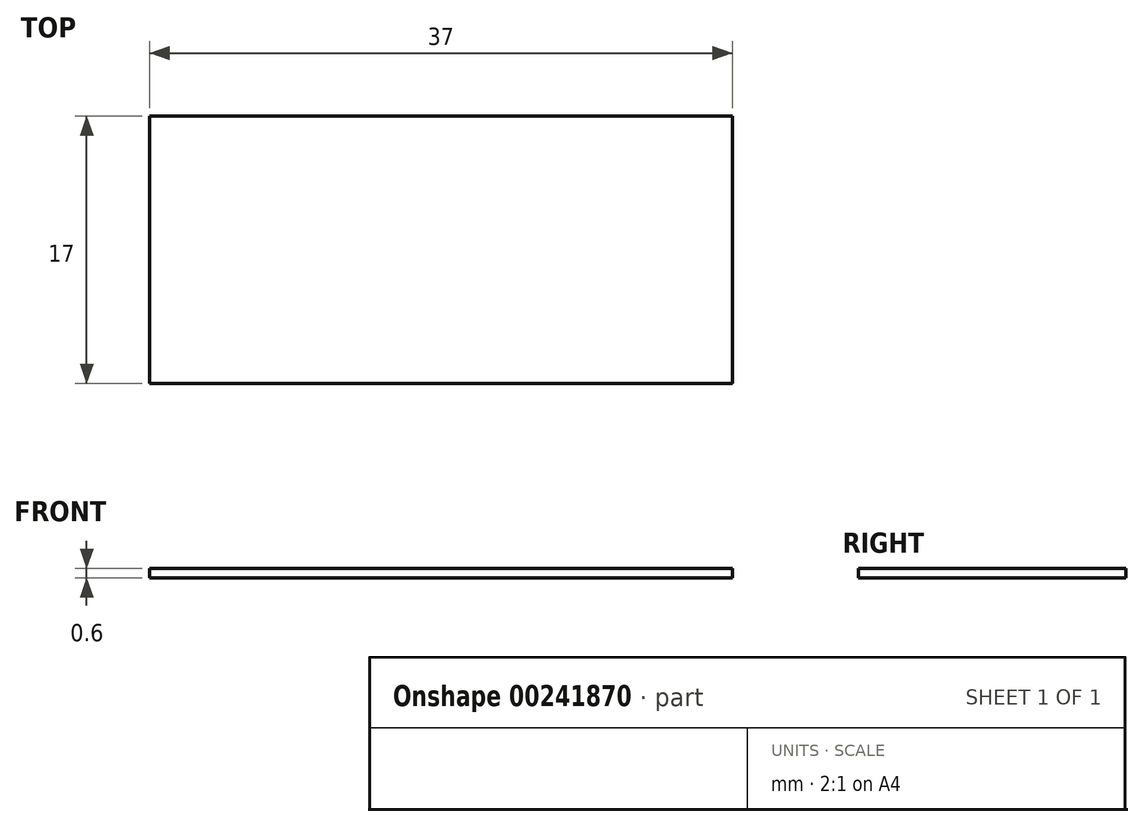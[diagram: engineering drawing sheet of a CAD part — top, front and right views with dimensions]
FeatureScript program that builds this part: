
annotation { "Feature Type Name" : "Feature", "Feature Type Description" : "" }
export const myFeature = defineFeature(function(context is Context, id is Id, definition is map)
    precondition{}
    {
        {
            var Q0;
            Q0=qCreatedBy(makeId("Top.planeOp"),FACE);
            var sketch = newSketch(context, id + "F0", { "sketchPlane" : qUnion([Q0])});
            skLineSegment(sketch, "E0.bottom", {"start": v(-37.58, 1.71) * mm, "end": v(-0.58, 1.71) * mm});
            skLineSegment(sketch, "E0.top", {"start": v(-37.58, -15.29) * mm, "end": v(-0.58, -15.29) * mm});
            skLineSegment(sketch, "E0.left", {"start": v(-37.58, 1.71) * mm, "end": v(-37.58, -15.29) * mm});
            skLineSegment(sketch, "E0.right", {"start": v(-0.58, 1.71) * mm, "end": v(-0.58, -15.29) * mm});
            skPoint(sketch, "E1.firstSnap0", {"position": v(-19.08, 1.71) * mm});
            skSolve(sketch);
        }
        {
            var Q0;
            Q0=makeQuery(id+"F0.imprint","IMPRINT",FACE,{"disambiguationData":[TD([[makeQuery(id+"F0.imprint","IMPRINT",EDGE,{"derivedFrom":sQuery(id+"F0.wireOp",EDGE,"E0.bottom")}),-1.0]])]});
            extrude(context, id + "F1", {"entities" : qUnion([Q0]), "depth" : .6 * mm, "offsetDistance" : 25 * mm});
        }
    });
